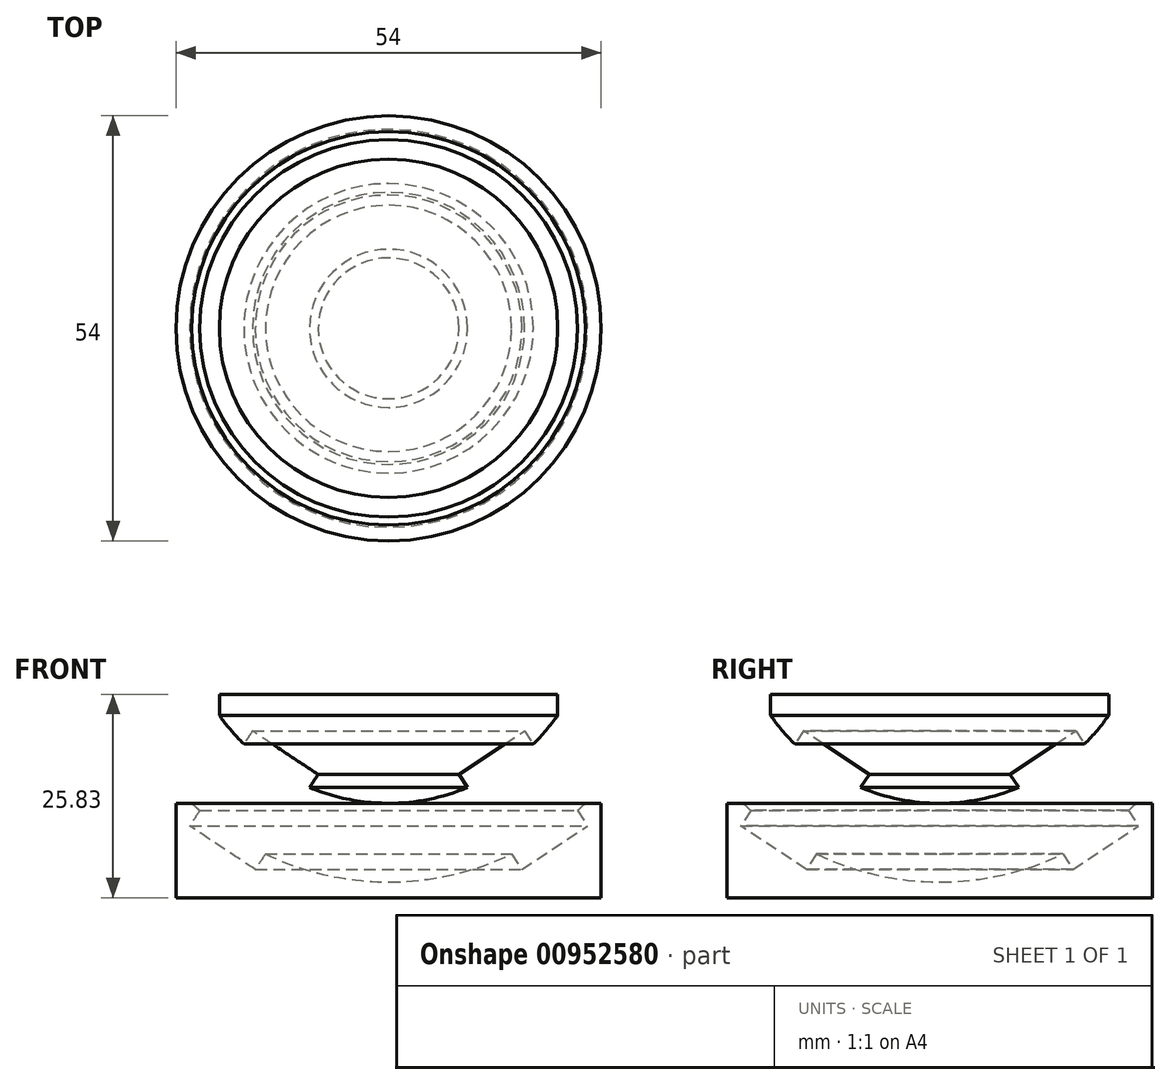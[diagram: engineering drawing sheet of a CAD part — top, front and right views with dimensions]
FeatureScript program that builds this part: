
annotation { "Feature Type Name" : "Feature", "Feature Type Description" : "" }
export const myFeature = defineFeature(function(context is Context, id is Id, definition is map)
    precondition{}
    {
        {
            assignVariable(context, id + "F0", {"name" : "magnetDepth", "anyValue" : 2});
        }
        {
            var Q0;
            Q0=qCreatedBy(makeId("Top.planeOp"),FACE);
            var sketch = newSketch(context, id + "F1", { "sketchPlane" : qUnion([Q0])});
            skCircle(sketch, "E0", {"center": v(0, 0) * mm, "radius": 5 * mm});
            skCircle(sketch, "E1", {"center": v(0, 0) * mm, "radius": 15 * mm});
            skSolve(sketch);
        }
        {
            var Q0;
            Q0=makeQuery(id+"F1.imprint","IMPRINT",FACE,{"disambiguationData":[TD([[makeQuery(id+"F1.imprint","IMPRINT",EDGE,{"derivedFrom":sQuery(id+"F1.wireOp",EDGE,"E0")}),1.0]])]});
            extrude(context, id + "F2", {"entities" : qUnion([Q0]), "depth" : (getVariable(context, 'magnetDepth')) * mm, "offsetDistance" : 25 * mm});
        }
        {
            var Q0;
            Q0=qCreatedBy(makeId("Front.planeOp"),FACE);
            var sketch = newSketch(context, id + "F3", { "sketchPlane" : qUnion([Q0])});
            skLineSegment(sketch, "E2", {"start": v(0, 0) * mm, "end": v(25, 0) * mm});
            skLineSegment(sketch, "E3", {"start": v(25, 0) * mm, "end": v(25, 12) * mm, "construction": true});
            skLineSegment(sketch, "E4", {"start": v(0, 0) * mm, "end": v(0, 2) * mm});
            skLineSegment(sketch, "E5", {"start": v(0, 2) * mm, "end": v(25, 2) * mm, "construction": true});
            skArc(sketch, "E6", {"start": v(0, 2) * mm, "mid": v(13.46, 4.6) * mm, "end": v(25, 12) * mm});
            skLineSegment(sketch, "E7", {"start": v(25, 12) * mm, "end": v(27, 12) * mm});
            skLineSegment(sketch, "E8", {"start": v(27, 12) * mm, "end": v(27, 0) * mm});
            skLineSegment(sketch, "E9", {"start": v(27, 0) * mm, "end": v(25, 0) * mm});
            skLineSegment(sketch, "E10.bottom", {"start": v(15.83, 5.26) * mm, "end": v(24.17, 10.78) * mm});
            skLineSegment(sketch, "E10.top", {"start": v(16.93, 3.59) * mm, "end": v(25.27, 9.1) * mm});
            skLineSegment(sketch, "E10.left", {"start": v(15.83, 5.26) * mm, "end": v(16.93, 3.59) * mm});
            skLineSegment(sketch, "E10.right", {"start": v(24.17, 10.78) * mm, "end": v(25.27, 9.1) * mm});
            skLineSegment(sketch, "E11", {"start": v(20, 8.02) * mm, "end": v(21.1, 6.35) * mm, "construction": true});
            skLineSegment(sketch, "E12", {"start": v(15.83, 5.26) * mm, "end": v(15.64, 5.55) * mm});
            skLineSegment(sketch, "E13", {"start": v(24.17, 10.78) * mm, "end": v(23.98, 11.06) * mm});
            skArc(sketch, "E14.0", {"start": v(0, 12) * mm, "mid": v(12.11, 14.96) * mm, "end": v(21.49, 23.17) * mm});
            skLineSegment(sketch, "E15", {"start": v(21.49, 23.17) * mm, "end": v(21.49, 25.83) * mm});
            skLineSegment(sketch, "E16", {"start": v(21.49, 25.83) * mm, "end": v(0, 25.83) * mm});
            skLineSegment(sketch, "E17", {"start": v(0, 25.83) * mm, "end": v(0, 12) * mm});
            skLineSegment(sketch, "E18.bottom", {"start": v(8.94, 15.67) * mm, "end": v(17.28, 21.18) * mm});
            skLineSegment(sketch, "E18.top", {"start": v(10.31, 13.6) * mm, "end": v(18.65, 19.12) * mm, "construction": true});
            skLineSegment(sketch, "E18.left", {"start": v(8.94, 15.67) * mm, "end": v(10.31, 13.6) * mm});
            skLineSegment(sketch, "E18.right", {"start": v(17.28, 21.18) * mm, "end": v(18.65, 19.12) * mm});
            skLineSegment(sketch, "E19", {"start": v(14.48, 16.36) * mm, "end": v(13.11, 18.43) * mm, "construction": true});
            skLineSegment(sketch, "E20", {"start": v(20, 8.02) * mm, "end": v(14.48, 16.36) * mm, "construction": true});
            skLineSegment(sketch, "E21", {"start": v(10.05, 14) * mm, "end": v(18.39, 19.52) * mm});
            skSolve(sketch);
        }
        {
            var Q0;
            Q0=makeQuery(id+"F3.imprint","IMPRINT",FACE,{"disambiguationData":[TD([[makeQuery(id+"F3.imprint","IMPRINT",EDGE,{"derivedFrom":sQuery(id+"F3.wireOp",EDGE,"E2")}),1.0]])]});
            var Q1;
            {var subQ0=sQuery(id+"F3.wireOp",EDGE,"E15");Q1=makeQuery(id+"F3.imprint","IMPRINT",FACE,{"disambiguationData":[TD([[makeQuery(id+"F3.imprint","IMPRINT",EDGE,{"derivedFrom":subQ0}),1.0]])]});}
            var Q2;
            Q2=sQuery(id+"F3.wireOp",EDGE,"E4");
            revolve(context, id + "F4", {"operationType" : NewBodyOperationType.ADD, "surfaceOperationType" : NewSurfaceOperationType.NEW, "entities" : qUnion([Q0, Q1]), "axis" : qUnion([Q2]), "revolveType" : RevolveType.FULL});
        }
    });
